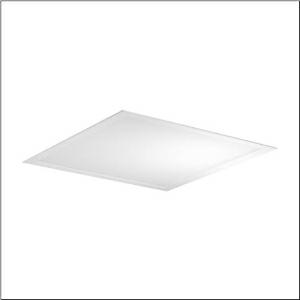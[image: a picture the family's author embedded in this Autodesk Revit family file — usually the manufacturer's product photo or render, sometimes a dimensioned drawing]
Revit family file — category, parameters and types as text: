
# Revit family: apollon_21_square_51mq11w72314
name_source: partatom
category: Lighting Fixtures
units: mm (PartAtom-declared; Revit-internal decimal feet)

## family parameters
Cut with Voids When Loaded = No
Host = Face
Light Source = No
Part Type = Normal
Room Calculation Point = No
Round Connector Dimension = Use Diameter
Shared = No

## types (1)
- Apollon 21 square (1 x LED, 4100 lm, 23.3 W, 3000K)
    Apparent Load = 23 VA
    CIE Flux Codes = 60 87 97 100 100
    Color Rendering = 80
    Color Temperature = 3000K
    Default Elevation = 1800 mm
    Description = Apollon 21 square, office luminaire, primary optical cover: micro prismatic cover, of PMMA, CAT 2 (L<= 3000cd/m²), light emission: direct distribution, primary light characteristic: symmetric, installation type: lay-in mounting, recessed, LED, rated luminous flux: 4.100lm, luminous efficacy: 176lm/W, light colour: 830, colour temperature: 3000K, control gear: ON/OFF, with terminal, 3-pole, mains connection: 220..240V, AC/DC, 0/50..60Hz, rated input power: 23.3W, suitable for self-contained emergency lighting element 59MQE002602A with integrated self-test function according to EN 60598-2-22, housing, of aluminium, coated, traffic white (RAL 9016), module: M625, length: 620mm, width: 620mm, height: 55mm, housing upper side, of sheet steel, galvanised, protection rating (complete): IP20, protection rating (lamp compartment, on room side): IP50, insulation class (complete): insulation class II (safety insulation), certification: CE, ENEC, UKCA, impact resistance: IK03, permissible operating ambient temperature: -20..+45°C, standard: EN 60598-2-22, corresponds to IFS (International Featured Standards) requirements for safety and quality in the food industry, packaging unit: 1 piece
    Height = 0 mm  [stored 0 ft]
    Lamp = 1 x LED
    Lamp Light Flux = 4100 lm
    Lamp Power = 23.3 W
    Lamp count = 1
    Length = 620 mm
    Luminous efficacy = 176 lm/W
    Manufacturer = Siteco
    ModVariant = No
    Model = 51MQ11W72314
    Mounting Place = Ceiling
    Mounting Type = Recessed
    Number of Poles = 1
    OnlyDefault = Yes
    Power Factor = 1
    Product Name = Apollon 21 square
    Product group = office luminaire | ceiling recessed
    ProductGroupID = 400
    Protection Class = Protection class II
    Protection Degree = IP 20
    RLX_Detail_Level = 1
    RLX_Emergency_Light_Flux = 0 lm
    RLX_Emergency_Type = 0
    RLX_Emergency_Type_DB = No
    RlxData = <blob elided: 13285 chars, md5=01f95cbd>
    Socket = socket
    Standby Power = 0 W
    System Light Flux = 4100 lm
    System Power = 23 W
    Type Comments = Product without accessories
    Type Image = l_1291054.jpg
    URL = http://relux.com
    VarID = ---
    Voltage = 0 V
    Weight = 0.00 kg
    Width = 620 mm

note: [stored X ft] marks values corroborated as IEEE doubles in the binary element streams (Revit-internal decimal feet)

## geometry (parser evidence)
native form markers: Sweep x10
no freeform markers — native parametric forms only
